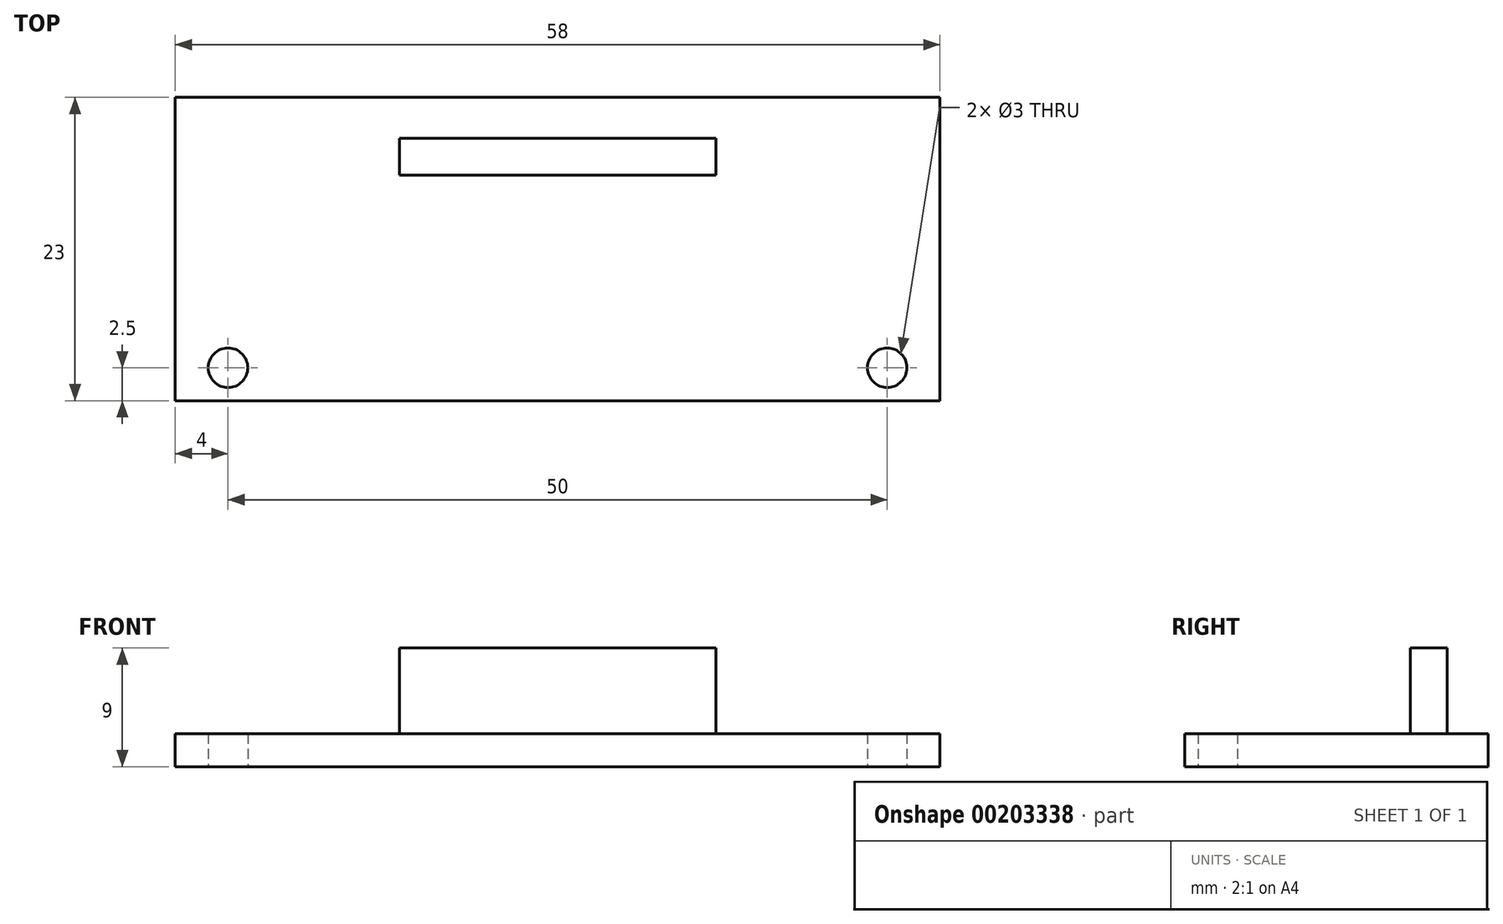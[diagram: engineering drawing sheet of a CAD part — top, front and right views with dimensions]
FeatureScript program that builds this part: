
annotation { "Feature Type Name" : "Feature", "Feature Type Description" : "" }
export const myFeature = defineFeature(function(context is Context, id is Id, definition is map)
    precondition{}
    {
        {
            var Q0;
            Q0=qCreatedBy(makeId("Top.planeOp"),FACE);
            var sketch = newSketch(context, id + "F0", { "sketchPlane" : qUnion([Q0])});
            skLineSegment(sketch, "E0.bottom", {"start": v(29, -11.5) * mm, "end": v(-29, -11.5) * mm});
            skLineSegment(sketch, "E0.top", {"start": v(29, 11.5) * mm, "end": v(-29, 11.5) * mm});
            skLineSegment(sketch, "E0.left", {"start": v(29, -11.5) * mm, "end": v(29, 11.5) * mm});
            skLineSegment(sketch, "E0.right", {"start": v(-29, -11.5) * mm, "end": v(-29, 11.5) * mm});
            skPoint(sketch, "E0.middle", {"position": v(0, 0) * mm});
            skLineSegment(sketch, "E1", {"start": v(-29, -9) * mm, "end": v(29, -9) * mm, "construction": true});
            skCircle(sketch, "E2", {"center": v(-25, -9) * mm, "radius": 1.5 * mm});
            skCircle(sketch, "E3", {"center": v(25, -9) * mm, "radius": 1.5 * mm});
            skSolve(sketch);
        }
        {
            var Q0;
            Q0 = qSketchRegion(id + "F0", true);
            extrude(context, id + "F1", {"entities" : qUnion([Q0]), "depth" : 2.5 * mm});
        }
        {
            var Q0;
            Q0=makeQuery(id+"F1.opExtrude","CAP_FACE",FACE,{"disambiguationData":[OSD([sQuery(id+"F0.wireOp",EDGE,"E0.bottom"),sQuery(id+"F0.wireOp",EDGE,"E0.top"),sQuery(id+"F0.wireOp",EDGE,"E0.left"),sQuery(id+"F0.wireOp",EDGE,"E0.right"),sQuery(id+"F0.wireOp",EDGE,"E2"),sQuery(id+"F0.wireOp",EDGE,"E3")])],"isStart":false});
            var sketch = newSketch(context, id + "F2", { "sketchPlane" : qUnion([Q0])});
            skLineSegment(sketch, "E4", {"start": v(29, 7) * mm, "end": v(-29, 7) * mm, "construction": true});
            skLineSegment(sketch, "E5.bottom", {"start": v(12, 5.6) * mm, "end": v(-12, 5.6) * mm});
            skLineSegment(sketch, "E5.top", {"start": v(12, 8.4) * mm, "end": v(-12, 8.4) * mm});
            skLineSegment(sketch, "E5.left", {"start": v(12, 5.6) * mm, "end": v(12, 8.4) * mm});
            skLineSegment(sketch, "E5.right", {"start": v(-12, 5.6) * mm, "end": v(-12, 8.4) * mm});
            skPoint(sketch, "E5.middle", {"position": v(0, 7) * mm});
            skSolve(sketch);
        }
        {
            var Q0;
            Q0 = qSketchRegion(id + "F2", true);
            extrude(context, id + "F3", {"entities" : qUnion([Q0]), "operationType" : NewBodyOperationType.ADD, "depth" : 6.5 * mm});
        }
    });
